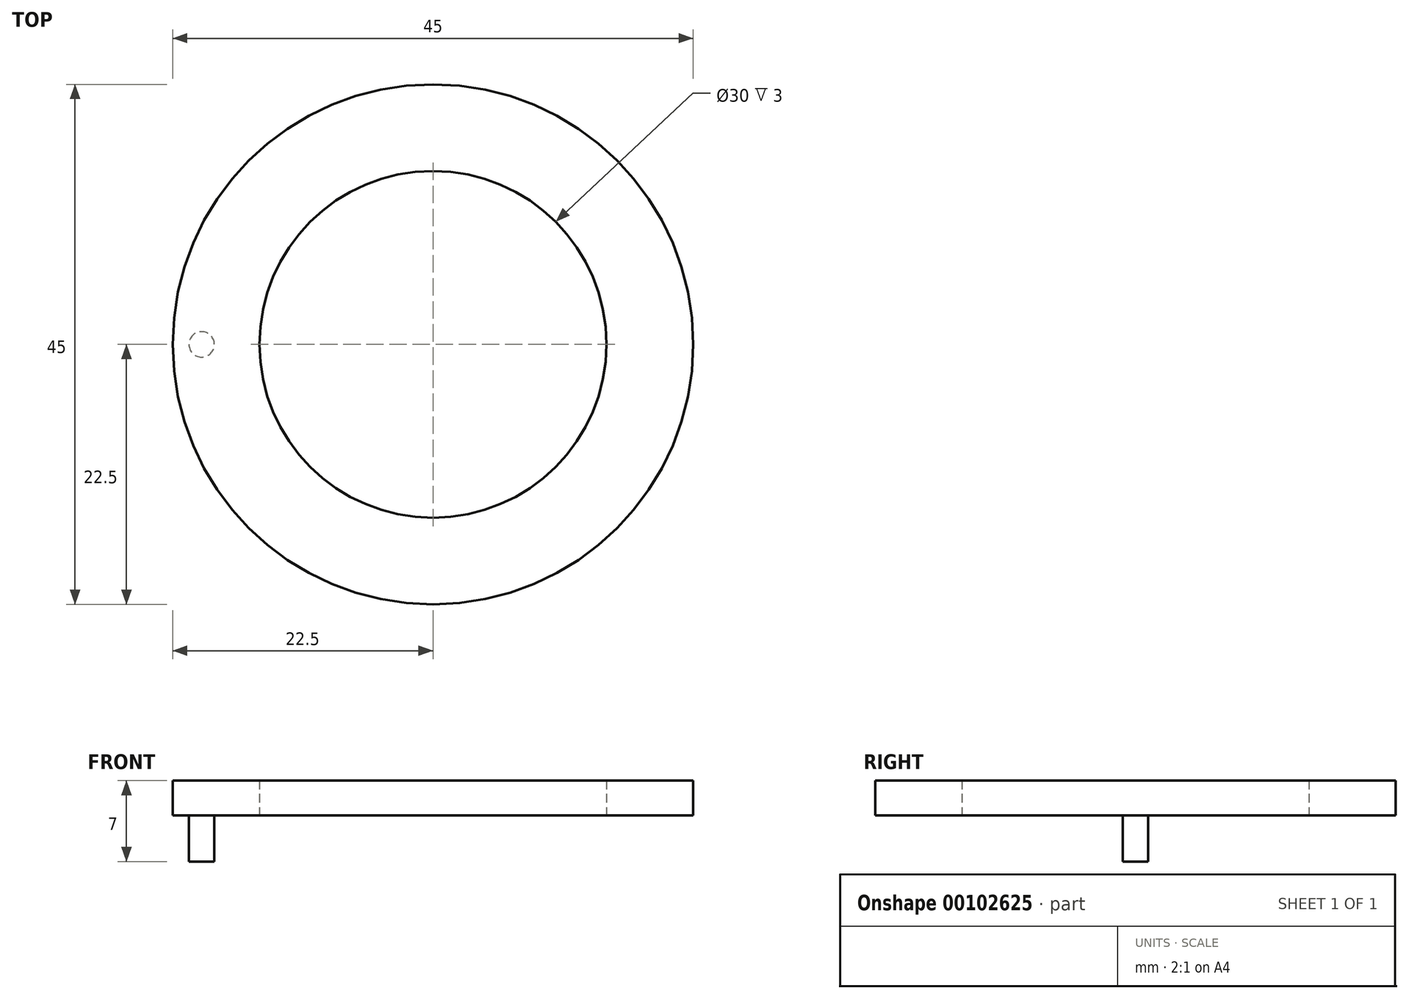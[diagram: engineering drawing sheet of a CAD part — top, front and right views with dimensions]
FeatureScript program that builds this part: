
annotation { "Feature Type Name" : "Feature", "Feature Type Description" : "" }
export const myFeature = defineFeature(function(context is Context, id is Id, definition is map)
    precondition{}
    {
        {
            var Q0;
            Q0=qCreatedBy(makeId("Top.planeOp"),FACE);
            var sketch = newSketch(context, id + "F0", { "sketchPlane" : qUnion([Q0])});
            skCircle(sketch, "E0", {"center": v(0, 0) * mm, "radius": 22.5 * mm});
            skCircle(sketch, "E1", {"center": v(0, 0) * mm, "radius": 15 * mm});
            skSolve(sketch);
        }
        {
            var Q0;
            Q0=makeQuery(id+"F0.imprint","IMPRINT",FACE,{"disambiguationData":[TD([[makeQuery(id+"F0.imprint","IMPRINT",EDGE,{"derivedFrom":sQuery(id+"F0.wireOp",EDGE,"E0")}),1.0]])]});
            extrude(context, id + "F1", {"entities" : qUnion([Q0]), "depth" : 3 * mm});
        }
        {
            var Q0;
            Q0=makeQuery(id+"F1.opExtrude","CAP_FACE",FACE,{"disambiguationData":[OSD([sQuery(id+"F0.wireOp",EDGE,"E0"),sQuery(id+"F0.wireOp",EDGE,"E1")])],"isStart":true});
            var sketch = newSketch(context, id + "F2", { "sketchPlane" : qUnion([Q0])});
            skCircle(sketch, "E2", {"center": v(-20, 0) * mm, "radius": 1.1 * mm});
            skSolve(sketch);
        }
        {
            var Q0;
            Q0=makeQuery(id+"F2.imprint","IMPRINT",FACE,{"disambiguationData":[TD([[makeQuery(id+"F2.imprint","IMPRINT",EDGE,{"derivedFrom":sQuery(id+"F2.wireOp",EDGE,"E2")}),1.0]])]});
            extrude(context, id + "F3", {"entities" : qUnion([Q0]), "operationType" : NewBodyOperationType.ADD, "depth" : 4 * mm});
        }
    });
